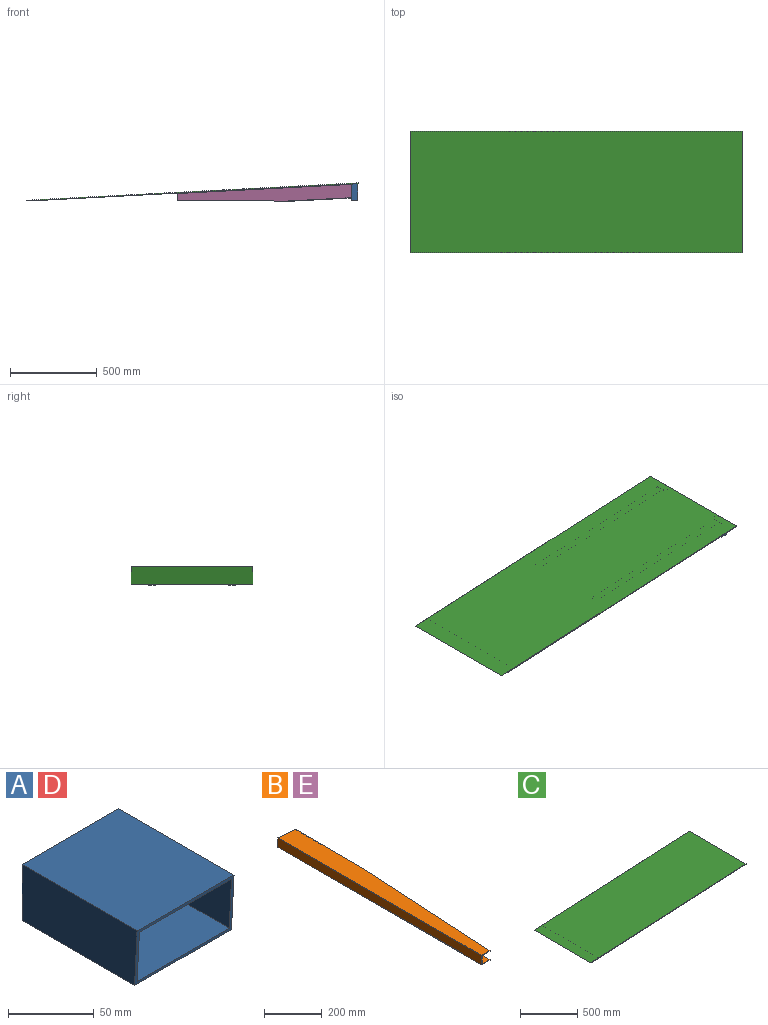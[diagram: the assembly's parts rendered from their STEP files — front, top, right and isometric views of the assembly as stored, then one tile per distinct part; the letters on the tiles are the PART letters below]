
ASSEMBLY  parts=5 mates=4
PART A: 10 faces, bbox 80x95x40 mm
  f0: plane 95x40mm, normal (1,0,0), area 3758.1mm2, adj f6,f7,f8,f9
  f1: plane 94.9x76mm, normal (0,0,-1), area 7212mm2, adj f2,f5,f8,f9
  f2: plane 94.9x36mm, normal (-1,0,0), area 3382.3mm2, adj f1,f3,f8,f9
  f3: plane 93.01x76mm, normal (0,0,1), area 7068.6mm2, adj f2,f5,f8,f9
  f4: plane 95x40mm, normal (-1,0,0), area 3758.1mm2, adj f6,f7,f8,f9
  f5: plane 94.9x36mm, normal (1,0,0), area 3382.3mm2, adj f1,f3,f8,f9
  f6: plane 95x80mm, normal (0,0,1), area 7600mm2, adj f0,f4,f8,f9
  f7: plane 92.9x80mm, normal (0,0,-1), area 7432.3mm2, adj f0,f4,f8,f9
  f8: plane 80x40mm, normal (0,1,0), area 464mm2, adj f0,f1,f2,f3,f4,f5,f6,f7
  f9: plane 80x40mm, normal (0,-1,-0.05), area 464.6mm2, adj f0,f1,f2,f3,f4,f5,f6,f7
PART B: 11 faces, bbox 80x1000x40 mm
  f0: plane 337.95x40mm, normal (1,0,0), area 13517.9mm2, adj f4,f7,f9,f10
  f1: plane 999.9x76mm, normal (0,0,-1), area 64294.4mm2, adj f2,f5,f6,f9,f10
  f2: plane 371.79x36mm, normal (-1,0,0), area 13384.4mm2, adj f1,f3,f9,f10
  f3: plane 999.9x76mm, normal (0,0,1), area 64294.4mm2, adj f2,f5,f6,f9,f10
  f4: plane 1000x80mm, normal (0,0,-1), area 67004mm2, adj f0,f6,f8,f9,f10
  f5: plane 999.9x36mm, normal (1,0,0), area 35996.2mm2, adj f1,f3,f6,f9
  f6: plane 41x40mm, normal (0,-1,0), area 236mm2, adj f1,f3,f4,f5,f7,f8,f10
  f7: plane 1000x80mm, normal (0,0,1), area 67004mm2, adj f0,f6,f8,f9,f10
  f8: plane 1000x40mm, normal (-1,0,0), area 40000mm2, adj f4,f6,f7,f9
  f9: plane 80x40mm, normal (0.05,1,0), area 464.6mm2, adj f0,f1,f2,f3,f4,f5,f7,f8
  f10: plane 657.86x40mm, normal (1,-0.06,0), area 3852.7mm2, adj f0,f1,f2,f3,f4,f6,f7
PART C: 6 faces, bbox 1908.1x700x100 mm
  f0: plane 1908.11x700mm, normal (-0.05,0,1), area 1337512.6mm2, adj f1,f3,f4,f5
  f1: plane 700x95.54mm, normal (0,0,-1), area 66875.6mm2, adj f0,f2,f4,f5
  f2: plane 1812.58x700mm, normal (0.05,0,-1), area 1270545.2mm2, adj f1,f3,f4,f5
  f3: plane 700x5.01mm, normal (1,0,0), area 3504.8mm2, adj f0,f2,f4,f5
  f4: plane 1908.11x100mm, normal (0,-1,0), area 9314.5mm2, adj f0,f1,f2,f3
  f5: plane 1908.11x100mm, normal (0,1,0), area 9314.5mm2, adj f0,f1,f2,f3
PART D: same geometry as A
PART E: same geometry as B
PLACE A rot(axis=(-0.58,0.58,-0.58),120deg) t=(1171.36,-194.64,-202.49)mm
PLACE B rot(axis=(0.6,0.57,-0.57),118.3deg) t=(1153.46,265.36,-149.53)mm
PLACE C t=(-616.21,385.36,-202.48)mm
PLACE D rot(axis=(-0.58,0.58,-0.58),120deg) t=(1171.36,265.36,-202.49)mm
PLACE E rot(axis=(0.6,0.57,-0.57),118.3deg) t=(1153.46,-194.64,-149.53)mm
MATE fastened B.f9 <-> D.f7  axis (1,0,0) through (1151.36,265.36,-109.58)mm
MATE fastened A.f9 <-> C.f2  axis (-0.05,0,1) through (1191.36,-194.64,-107.49)mm
MATE fastened E.f9 <-> A.f7  axis (1,0,0) through (1151.36,-194.64,-109.58)mm
MATE fastened D.f9 <-> C.f2  axis (-0.05,0,1) through (1191.36,265.36,-107.49)mm
